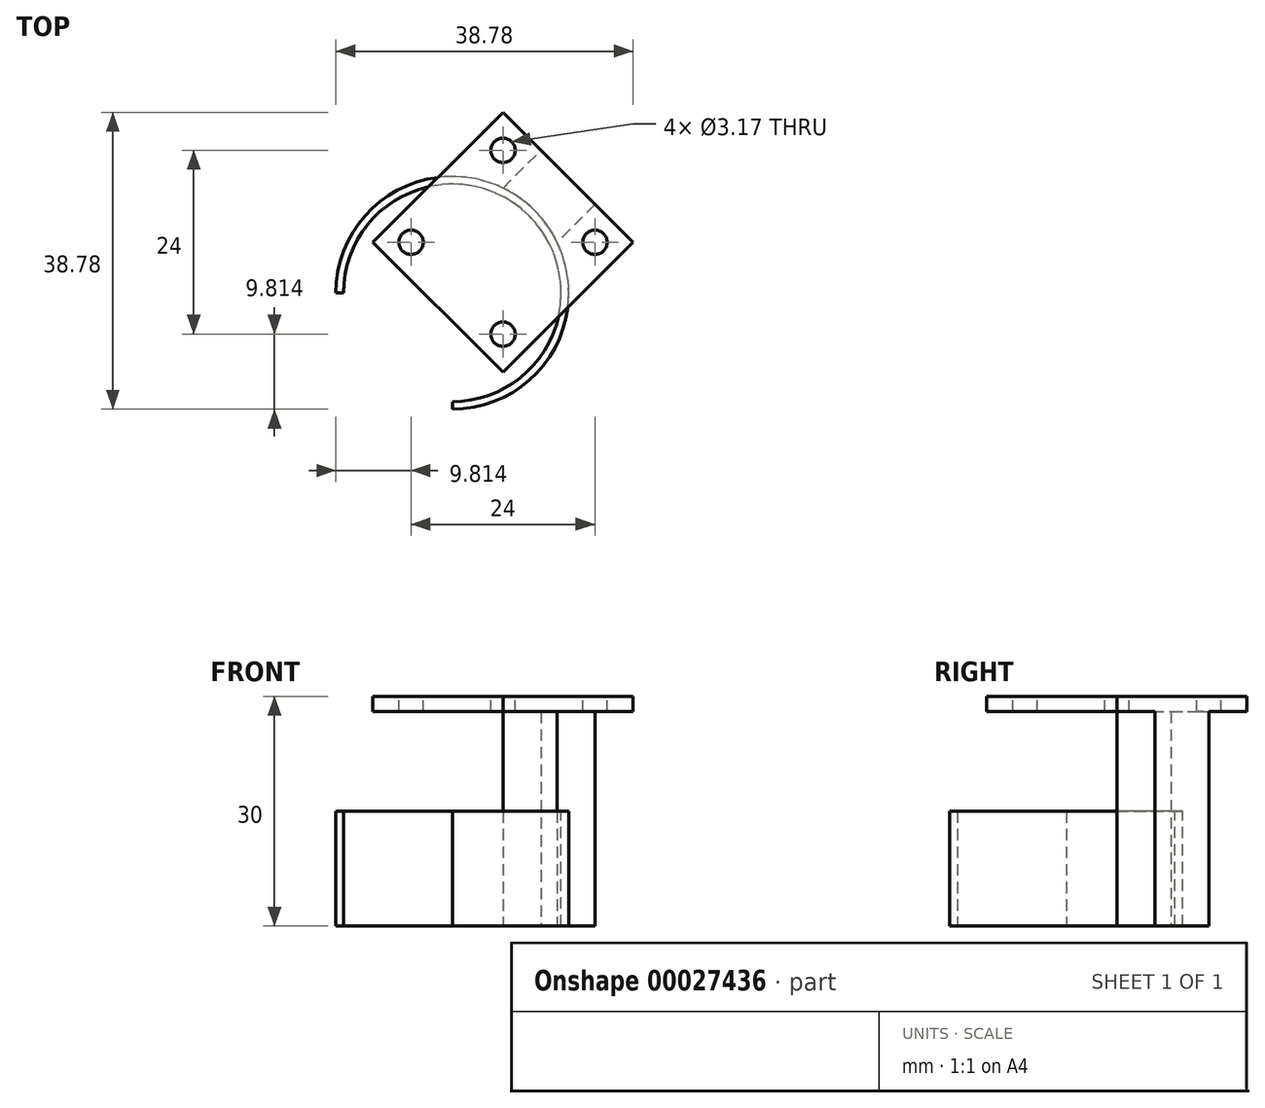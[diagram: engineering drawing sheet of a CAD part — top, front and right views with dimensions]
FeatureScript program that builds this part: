
annotation { "Feature Type Name" : "Feature", "Feature Type Description" : "" }
export const myFeature = defineFeature(function(context is Context, id is Id, definition is map)
    precondition{}
    {
        {
            var Q0;
            Q0=qCreatedBy(makeId("Front.planeOp"),FACE);
            var sketch = newSketch(context, id + "F0", { "sketchPlane" : qUnion([Q0])});
            skLineSegment(sketch, "E0.bottom", {"start": v(-15.2, 15) * mm, "end": v(-14.2, 15) * mm});
            skLineSegment(sketch, "E0.top", {"start": v(-15.2, 0) * mm, "end": v(-14.2, 0) * mm});
            skLineSegment(sketch, "E0.left", {"start": v(-15.2, 15) * mm, "end": v(-15.2, 0) * mm});
            skLineSegment(sketch, "E0.right", {"start": v(-14.2, 15) * mm, "end": v(-14.2, 0) * mm});
            skLineSegment(sketch, "E1", {"start": v(0, 14.86) * mm, "end": v(0, -11) * mm, "construction": true});
            skSolve(sketch);
        }
        {
            var Q0;
            Q0=makeQuery(id+"F0.imprint","IMPRINT",FACE,{"disambiguationData":[TD([[makeQuery(id+"F0.imprint","IMPRINT",EDGE,{"derivedFrom":sQuery(id+"F0.wireOp",EDGE,"E0.bottom")}),-1.0]])]});
            var Q1;
            Q1=sQuery(id+"F0.wireOp",EDGE,"E1");
            revolve(context, id + "F1", {"entities" : qUnion([Q0]), "axis" : qUnion([Q1]), "revolveType" : RevolveType.ONE_DIRECTION, "angle" : 270 * degree});
        }
        {
            var Q0;
            Q0=makeQuery(id+"F1.opRevolve","SWEPT_FACE",FACE,{"disambiguationData":[OSD([sQuery(id+"F0.wireOp",EDGE,"E0.bottom")])]});
            var sketch = newSketch(context, id + "F2", { "sketchPlane" : qUnion([Q0])});
            skLineSegment(sketch, "E2", {"start": v(6.61, 13.69) * mm, "end": v(11.56, 18.64) * mm});
            skLineSegment(sketch, "E3", {"start": v(11.56, 18.64) * mm, "end": v(18.64, 11.56) * mm});
            skLineSegment(sketch, "E4", {"start": v(18.64, 11.56) * mm, "end": v(13.69, 6.61) * mm});
            skLineSegment(sketch, "E5", {"start": v(13.69, 6.61) * mm, "end": v(0, -15.2) * mm, "construction": true});
            skLineSegment(sketch, "E6", {"start": v(6.61, 13.69) * mm, "end": v(-15.2, 0) * mm, "construction": true});
            skSolve(sketch);
        }
        {
            var Q0;
            {var subQ0=sQuery(id+"F2.wireOp",EDGE,"E2");Q0=makeQuery(id+"F2.imprint","IMPRINT",FACE,{"disambiguationData":[TD([[makeQuery(id+"F2.imprint","IMPRINT",EDGE,{"derivedFrom":subQ0}),-1.0]])]});}
            extrude(context, id + "F3", {"entities" : qUnion([Q0]), "depth" : 30 * mm, "symmetric" : true});
        }
        {
            var Q0;
            Q0=makeQuery(id+"F3.opExtrude","CAP_FACE",FACE,{"disambiguationData":[OSD([sQuery(id+"F0.wireOp",EDGE,"E0.bottom"),sQuery(id+"F0.wireOp",EDGE,"E0.left"),sQuery(id+"F2.wireOp",EDGE,"E2"),sQuery(id+"F2.wireOp",EDGE,"E3"),sQuery(id+"F2.wireOp",EDGE,"E4")])],"isStart":false});
            var sketch = newSketch(context, id + "F4", { "sketchPlane" : qUnion([Q0])});
            skLineSegment(sketch, "E7", {"start": v(18.64, 11.56) * mm, "end": v(23.58, 6.61) * mm});
            skLineSegment(sketch, "E8", {"start": v(11.56, 18.64) * mm, "end": v(6.61, 23.58) * mm});
            skLineSegment(sketch, "E9", {"start": v(23.58, 6.61) * mm, "end": v(6.61, -10.36) * mm});
            skLineSegment(sketch, "E10", {"start": v(6.61, -10.36) * mm, "end": v(-10.36, 6.61) * mm});
            skLineSegment(sketch, "E11", {"start": v(-10.36, 6.61) * mm, "end": v(6.61, 23.58) * mm});
            skLineSegment(sketch, "E12.2", {"start": v(11.56, 18.64) * mm, "end": v(18.64, 11.56) * mm});
            skSolve(sketch);
        }
        {
            var Q0;
            Q0=makeQuery(id+"F4.imprint","IMPRINT",FACE,{"disambiguationData":[TD([[makeQuery(id+"F4.imprint","IMPRINT",EDGE,{"derivedFrom":sQuery(id+"F4.wireOp",EDGE,"E7")}),-1.0]])]});
            var Q1;
            Q1=makeQuery(id+"F4.imprint","IMPRINT",FACE,{"disambiguationData":[TD([[makeQuery(id+"F4.imprint","IMPRINT",EDGE,{"derivedFrom":sQuery(id+"F4.wireOp",EDGE,"E12.2")}),-1.0]])]});
            extrude(context, id + "F5", {"entities" : qUnion([Q0, Q1]), "operationType" : NewBodyOperationType.ADD, "oppositeDirection" : true, "depth" : 2 * mm});
        }
        {
            var Q0;
            Q0=makeQuery(id+"F5.boolean.opBoolean","MERGE",FACE,{"derivedFrom":[makeQuery(id+"F3.opExtrude","CAP_FACE",FACE,{"disambiguationData":[OSD([sQuery(id+"F0.wireOp",EDGE,"E0.bottom"),sQuery(id+"F0.wireOp",EDGE,"E0.left"),sQuery(id+"F2.wireOp",EDGE,"E2"),sQuery(id+"F2.wireOp",EDGE,"E3"),sQuery(id+"F2.wireOp",EDGE,"E4")])],"isStart":false}),makeQuery(id+"F5.opExtrude","CAP_FACE",FACE,{"disambiguationData":[OSD([sQuery(id+"F4.wireOp",EDGE,"E7"),sQuery(id+"F4.wireOp",EDGE,"E8"),sQuery(id+"F4.wireOp",EDGE,"E9"),sQuery(id+"F4.wireOp",EDGE,"E10"),sQuery(id+"F4.wireOp",EDGE,"E11"),sQuery(id+"F4.wireOp",EDGE,"E12.2")])],"isStart":true})]});
            var sketch = newSketch(context, id + "F6", { "sketchPlane" : qUnion([Q0])});
            skLineSegment(sketch, "E13", {"start": v(6.61, 23.58) * mm, "end": v(6.61, -10.36) * mm, "construction": true});
            skLineSegment(sketch, "E14", {"start": v(23.58, 6.61) * mm, "end": v(-10.36, 6.61) * mm, "construction": true});
            skCircle(sketch, "E15", {"center": v(6.61, 18.61) * mm, "radius": 1.59 * mm});
            skCircle(sketch, "E16", {"center": v(18.61, 6.61) * mm, "radius": 1.59 * mm});
            skCircle(sketch, "E17", {"center": v(6.61, -5.39) * mm, "radius": 1.59 * mm});
            skCircle(sketch, "E18", {"center": v(-5.39, 6.61) * mm, "radius": 1.59 * mm});
            skSolve(sketch);
        }
        {
            var Q0;
            Q0=makeQuery(id+"F6.imprint","IMPRINT",FACE,{"disambiguationData":[TD([[makeQuery(id+"F6.imprint","IMPRINT",EDGE,{"derivedFrom":sQuery(id+"F6.wireOp",EDGE,"E16")}),1.0]])]});
            var Q1;
            Q1=makeQuery(id+"F6.imprint","IMPRINT",FACE,{"disambiguationData":[TD([[makeQuery(id+"F6.imprint","IMPRINT",EDGE,{"derivedFrom":sQuery(id+"F6.wireOp",EDGE,"E15")}),1.0]])]});
            var Q2;
            Q2=makeQuery(id+"F6.imprint","IMPRINT",FACE,{"disambiguationData":[TD([[makeQuery(id+"F6.imprint","IMPRINT",EDGE,{"derivedFrom":sQuery(id+"F6.wireOp",EDGE,"E17")}),1.0]])]});
            var Q3;
            Q3=makeQuery(id+"F6.imprint","IMPRINT",FACE,{"disambiguationData":[TD([[makeQuery(id+"F6.imprint","IMPRINT",EDGE,{"derivedFrom":sQuery(id+"F6.wireOp",EDGE,"E18")}),1.0]])]});
            var Q4;
            Q4=makeQuery(id+"F5.opExtrude","CAP_FACE",FACE,{"disambiguationData":[OSD([sQuery(id+"F4.wireOp",EDGE,"E7"),sQuery(id+"F4.wireOp",EDGE,"E8"),sQuery(id+"F4.wireOp",EDGE,"E9"),sQuery(id+"F4.wireOp",EDGE,"E10"),sQuery(id+"F4.wireOp",EDGE,"E11"),sQuery(id+"F4.wireOp",EDGE,"E12.2")])],"isStart":false});
            extrude(context, id + "F7", {"entities" : qUnion([Q0, Q1, Q2, Q3]), "operationType" : NewBodyOperationType.REMOVE, "endBound" : BoundingType.UP_TO_SURFACE, "oppositeDirection" : true, "endBoundEntityFace" : qUnion([Q4]), "depth" : 25 * mm});
        }
    });
